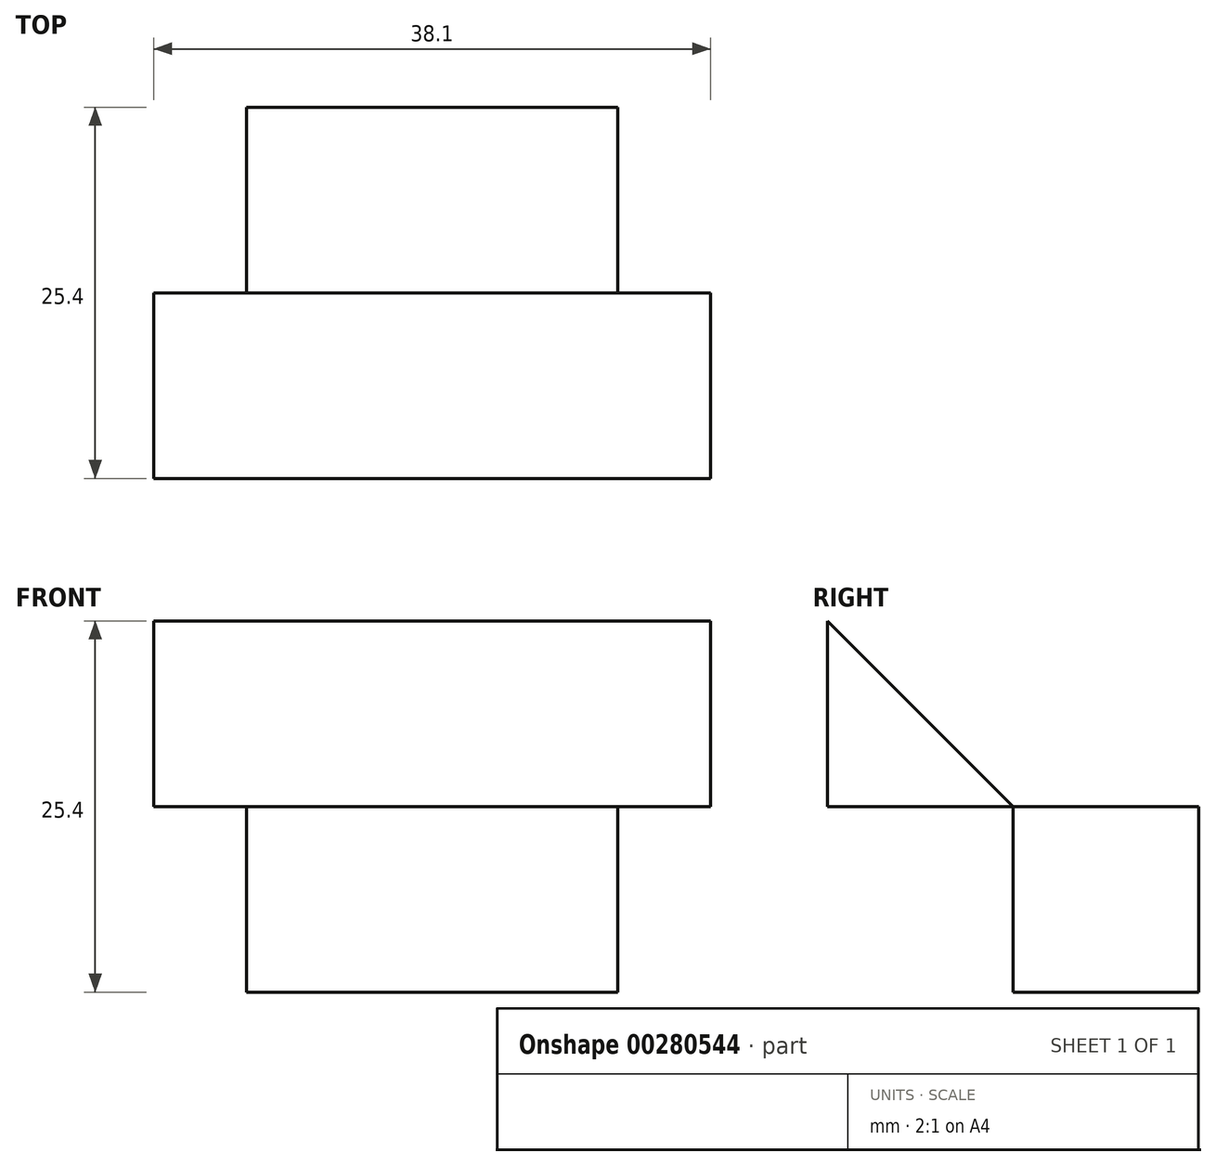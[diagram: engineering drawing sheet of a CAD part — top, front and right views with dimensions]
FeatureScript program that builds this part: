
annotation { "Feature Type Name" : "Feature", "Feature Type Description" : "" }
export const myFeature = defineFeature(function(context is Context, id is Id, definition is map)
    precondition{}
    {
        {
            var Q0;
            Q0=qCreatedBy(makeId("Top.planeOp"),FACE);
            var sketch = newSketch(context, id + "F0", { "sketchPlane" : qUnion([Q0])});
            skLineSegment(sketch, "E0", {"start": v(0, 0) * mm, "end": v(0, -25.4) * mm});
            skLineSegment(sketch, "E1", {"start": v(0, -25.4) * mm, "end": v(38.1, -25.4) * mm});
            skLineSegment(sketch, "E2", {"start": v(38.1, -25.4) * mm, "end": v(38.1, 0) * mm});
            skLineSegment(sketch, "E3", {"start": v(38.1, 0) * mm, "end": v(0, 0) * mm});
            skLineSegment(sketch, "E4", {"start": v(38.1, 0) * mm, "end": v(31.75, 0) * mm});
            skLineSegment(sketch, "E5", {"start": v(31.75, 0) * mm, "end": v(31.75, -12.7) * mm});
            skLineSegment(sketch, "E6", {"start": v(31.75, -12.7) * mm, "end": v(6.35, -12.7) * mm});
            skLineSegment(sketch, "E7", {"start": v(6.35, -12.7) * mm, "end": v(6.35, 0) * mm});
            skLineSegment(sketch, "E8", {"start": v(0, 0) * mm, "end": v(6.35, 0) * mm});
            skSolve(sketch);
        }
        {
            var Q0;
            Q0 = qSketchRegion(id + "F0", true);
            extrude(context, id + "F1", {"entities" : qUnion([Q0]), "depth" : 25.4 * mm});
        }
        {
            var Q0;
            Q0=makeQuery(id+"F0.imprint","IMPRINT",FACE,{"disambiguationData":[TD([[makeQuery(id+"F0.imprint","IMPRINT",EDGE,{"derivedFrom":sQuery(id+"F0.wireOp",EDGE,"E3")}),1.0]])]});
            extrude(context, id + "F2", {"entities" : qUnion([Q0]), "operationType" : NewBodyOperationType.REMOVE, "depth" : 12.7 * mm});
        }
        {
            var Q0;
            Q0=makeQuery(id+"F1.opExtrude","SWEPT_FACE",FACE,{"disambiguationData":[OSD([sQuery(id+"F0.wireOp",EDGE,"E0")])]});
            var sketch = newSketch(context, id + "F3", { "sketchPlane" : qUnion([Q0])});
            skLineSegment(sketch, "E9", {"start": v(0, 0) * mm, "end": v(0, 25.4) * mm});
            skLineSegment(sketch, "E10", {"start": v(0, 25.4) * mm, "end": v(25.4, 25.4) * mm});
            skLineSegment(sketch, "E11", {"start": v(25.4, 25.4) * mm, "end": v(0, 0) * mm});
            skSolve(sketch);
        }
        {
            var Q0;
            Q0=makeQuery(id+"F3.imprint","IMPRINT",FACE,{"disambiguationData":[TD([[makeQuery(id+"F3.imprint","IMPRINT",EDGE,{"derivedFrom":sQuery(id+"F3.wireOp",EDGE,"E9")}),1.0]])]});
            extrude(context, id + "F4", {"entities" : qUnion([Q0]), "operationType" : NewBodyOperationType.REMOVE, "oppositeDirection" : true, "depth" : 38.1 * mm});
        }
    });
